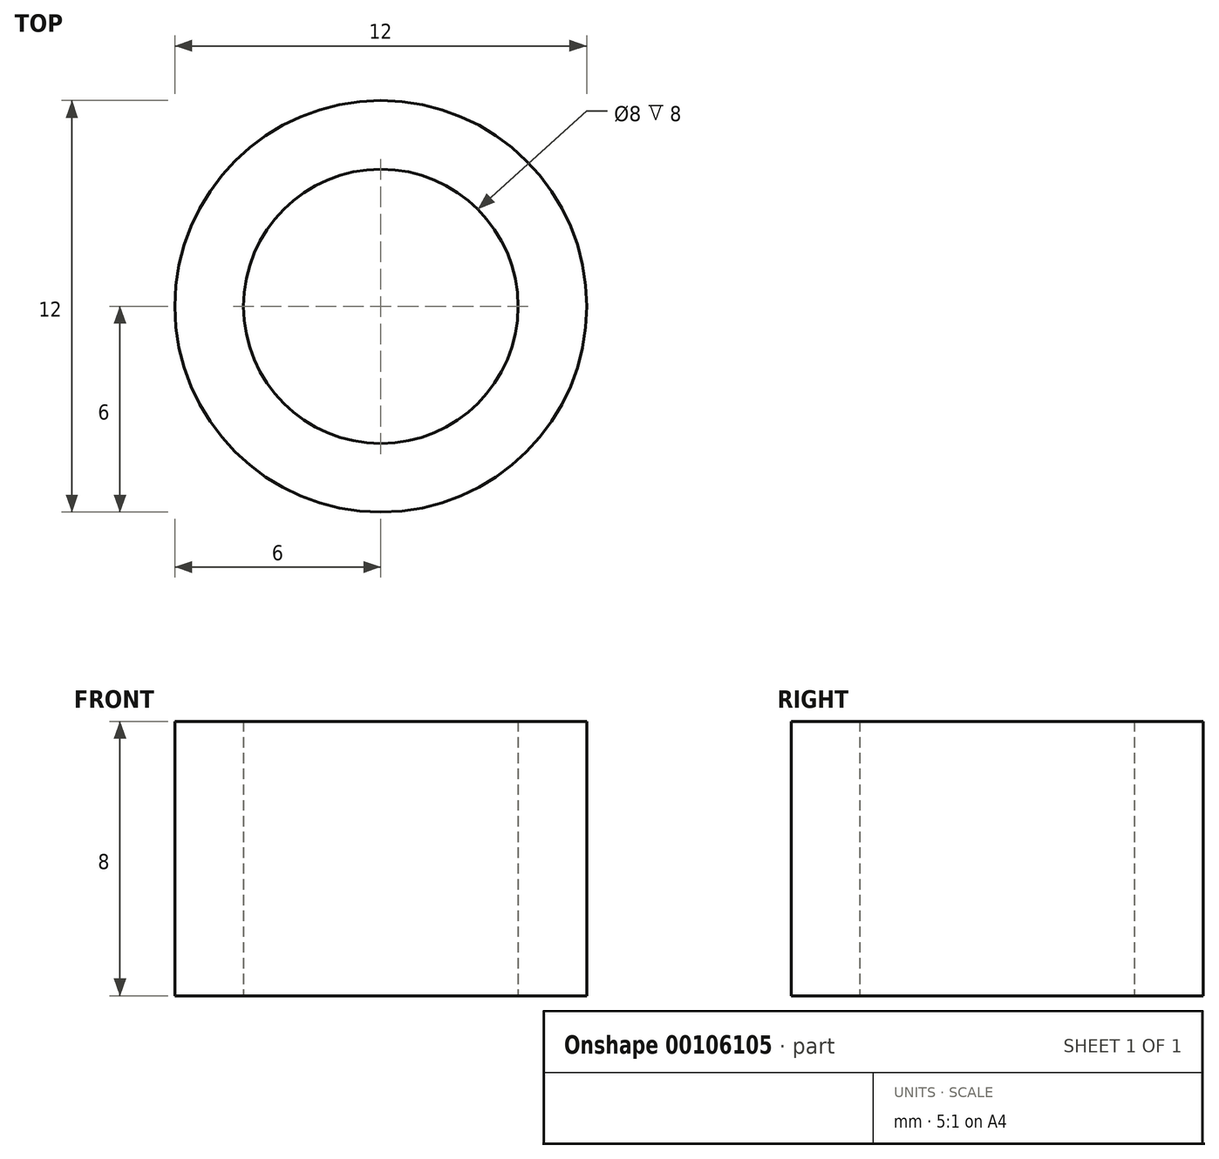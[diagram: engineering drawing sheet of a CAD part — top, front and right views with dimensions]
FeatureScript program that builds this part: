
annotation { "Feature Type Name" : "Feature", "Feature Type Description" : "" }
export const myFeature = defineFeature(function(context is Context, id is Id, definition is map)
    precondition{}
    {
        {
            var Q0;
            Q0=qCreatedBy(makeId("Top.planeOp"),FACE);
            var sketch = newSketch(context, id + "F0", { "sketchPlane" : qUnion([Q0])});
            skCircle(sketch, "E0", {"center": v(0, 0) * mm, "radius": 6 * mm});
            skCircle(sketch, "E1", {"center": v(0, 0) * mm, "radius": 4 * mm});
            skSolve(sketch);
        }
        {
            var Q0;
            Q0=makeQuery(id+"F0.imprint","IMPRINT",FACE,{"disambiguationData":[TD([[makeQuery(id+"F0.imprint","IMPRINT",EDGE,{"derivedFrom":sQuery(id+"F0.wireOp",EDGE,"E0")}),1.0]])]});
            extrude(context, id + "F1", {"entities" : qUnion([Q0]), "depth" : 8 * mm});
        }
    });
